# Revit family: 204_FLEXIT SC60-_
name_source: partatom
category: Duct Accessories
units: mm (PartAtom-declared; Revit-internal decimal feet)

## family parameters
Always vertical = Yes
Cut with Voids When Loaded = No
Part Type = Damper
Round Connector Dimension = Use Diameter
Shared = No
Work Plane-Based = No

## types (4) — shared parameters
CAT0 = Yes
Description = Damper fire retardant SC60
H2D = 100 mm  [stored 0.328084 ft]
L = 40 mm  [stored 0.131234 ft]
L2D = 40 mm  [stored 0.131234 ft]
LT2 = 20 mm  [stored 0.0656168 ft]
Manufacturer = Flexit
QmdConnectorList = 201;D;202;D
W2D = 100 mm  [stored 0.328084 ft]
magiPartTypeId = 204
magiProductFamilyId = FLEXIT SC60-*

## per-type parameters (varying)
| type | D | DT2 | H | R1 | magiProductId |
| 100-114515 | 100 mm | 50 mm | 100 mm  [stored 0.328084 ft] | 49 mm | FLEXIT SC60-100 |
| 125-114516 | 125 mm | 63 mm | 125 mm | 62 mm | FLEXIT SC60-125 |
| 160-114517 | 160 mm | 80 mm | 160 mm | 79 mm | FLEXIT SC60-160 |
| 200-114518 | 200 mm | 100 mm  [stored 0.328084 ft] | 200 mm  [stored 0.656168 ft] | 99 mm | FLEXIT SC60-200 |

note: column(s) folded — value = type name in every type: MC Product Code

note: [stored X ft] marks values corroborated as IEEE doubles in the binary element streams (Revit-internal decimal feet)

## geometry (parser evidence)
native form markers: Sweep x2
no freeform markers — native parametric forms only
